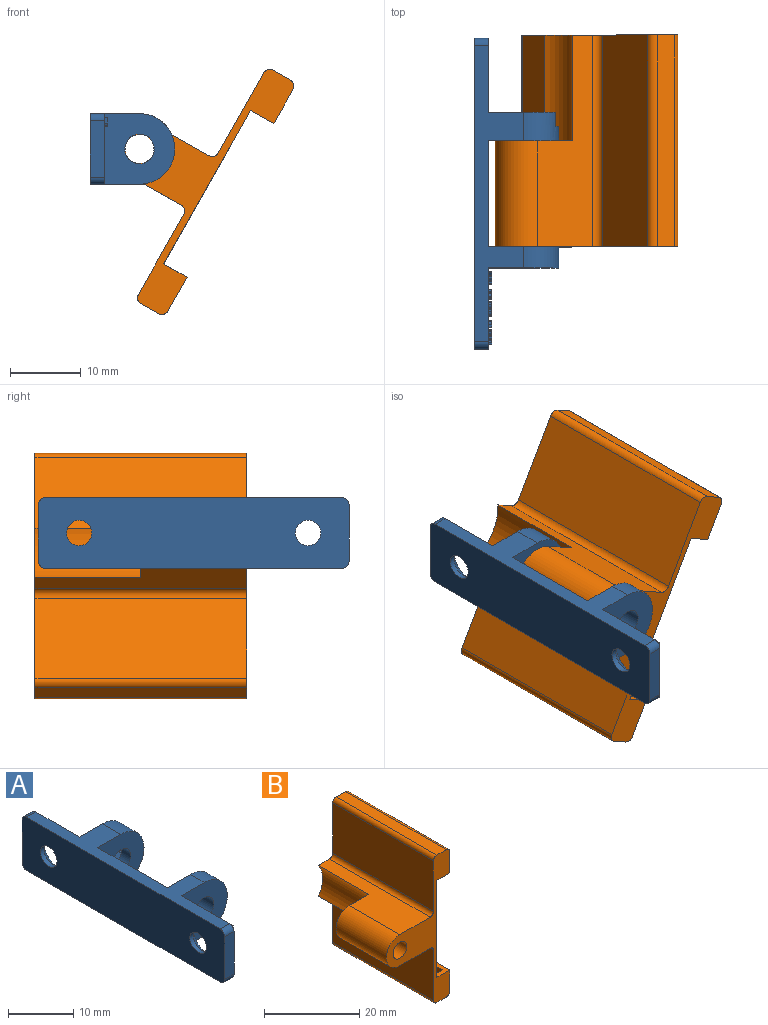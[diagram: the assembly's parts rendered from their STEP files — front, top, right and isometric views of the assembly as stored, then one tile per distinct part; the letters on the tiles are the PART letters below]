
ASSEMBLY  parts=2 mates=1
PART A: 199 faces, bbox 12x44x10 mm
  f0: plane 11.48x10mm, normal (1,0,0), area 80.2mm2, adj f4,f5,f6,f7,f8,f11,f28,f32
  f1: plane 15.05x10mm, normal (1,0,0), area 150.5mm2, adj f4,f8,f17,f29
  f2: plane 10x9.58mm, normal (0,1,0), area 42.1mm2, adj f3,f4,f8,f18,f19,f20,f21,f22
  f3: plane 10.48x10mm, normal (1,0,0), area 76mm2, adj f2,f4,f8,f12,f13,f14,f16
  f4: plane 42x7mm, normal (0,0,1), area 119mm2, adj f0,f1,f2,f3,f5,f9,f12,f17
  f5: cylinder r=1mm len=2mm, axis (-1,0,0), area 3.1mm2, adj f0,f4,f6,f9
  f6: plane 8x2mm, normal (0,-1,0), area 16mm2, adj f0,f5,f7,f9
  f7: cylinder r=1mm len=2mm, axis (-1,0,0), area 3.1mm2, adj f0,f6,f8,f9
  f8: plane 42x7mm, normal (0,0,-1), area 119mm2, adj f0,f1,f2,f3,f7,f9,f14,f17
  f9: plane 44x10mm, normal (-1,0,0), area 418.8mm2, adj f4,f5,f6,f7,f8,f10,f12,f13
  f10: cylinder r=1.8mm len=3.6mm, axis (1,0,0), area 9mm2, adj f9,f11
  f11: cone r=1.8mm half-angle=45deg, axis (1,0,0), area 25.6mm2, adj f0,f10
  f12: cylinder r=1mm len=2mm, axis (-1,0,0), area 3.1mm2, adj f3,f4,f9,f13
  f13: plane 8x2mm, normal (0,1,0), area 16mm2, adj f3,f9,f12,f14
  f14: cylinder r=1mm len=2mm, axis (-1,0,0), area 3.1mm2, adj f3,f8,f9,f13
  f15: cylinder r=1.8mm len=3.6mm, axis (1,0,0), area 9mm2, adj f9,f16
  f16: cone r=1.8mm half-angle=45deg, axis (1,0,0), area 25.6mm2, adj f3,f15
  f17: plane 10x10mm, normal (0,-1,0), area 75.4mm2, adj f1,f4,f8,f26,f27
  f18: plane 3.46x2mm, normal (-0.5,0,-0.87), area 8mm2, adj f2,f19,f24,f25
  f19: plane 2x1.12mm, normal (0,0,-1), area 2.2mm2, adj f2,f18,f25,f27
  f20: plane 2x1.12mm, normal (0,0,1), area 2.2mm2, adj f2,f21,f25,f27
  f21: plane 3.46x2mm, normal (-0.5,0,0.87), area 8mm2, adj f2,f20,f22,f25
  f22: plane 3.46x2mm, normal (0.5,0,0.87), area 8mm2, adj f2,f21,f23,f25
  f23: plane 4x2mm, normal (1,0,0), area 8mm2, adj f2,f22,f24,f25
  f24: plane 3.46x2mm, normal (0.5,0,-0.87), area 8mm2, adj f2,f18,f23,f25
  f25: plane 8.46x8mm, normal (0,1,0), area 33.3mm2, adj f18,f19,f20,f21,f22,f23,f24,f26
  f26: cylinder r=2.1mm len=4.2mm, axis (0,1,0), area 26.4mm2, adj f17,f25
  f27: cylinder r=5mm len=10mm, axis (0,1,0), area 54.6mm2, adj f2,f4,f8,f17,f19,f20,f25
  f28: plane 10x10mm, normal (0,-1,0), area 75.4mm2, adj f0,f4,f8,f30,f31
  f29: plane 10x10mm, normal (0,1,0), area 75.4mm2, adj f1,f4,f8,f30,f31
  f30: cylinder r=5mm len=10mm, axis (0,1,0), area 47.1mm2, adj f4,f8,f28,f29
  f31: cylinder r=2.1mm len=4.2mm, axis (0,1,0), area 39.6mm2, adj f28,f29
  f32: plane 0.84x0.5mm, normal (0,1,0), area 0.4mm2, adj f0,f33,f46,f47
  f33: plane 0.5x0.27mm, normal (0,0,1), area 0.1mm2, adj f0,f32,f34,f47
  f34: plane 0.79x0.5mm, normal (0,-1,0), area 0.4mm2, adj f0,f33,f35,f47
  f35: extruded ~0.5x0.22mm, area 0.1mm2, adj f0,f34,f36,f47
  f36: extruded ~0.5x0.2mm, area 0.1mm2, adj f0,f35,f37,f47
  f37: extruded ~0.5x0.2mm, area 0.1mm2, adj f0,f36,f38,f47
  f38: extruded ~0.5x0.22mm, area 0.1mm2, adj f0,f37,f39,f47
  f39: plane 0.79x0.5mm, normal (0,1,0), area 0.4mm2, adj f0,f38,f40,f47
  f40: plane 0.5x0.27mm, normal (0,0,1), area 0.1mm2, adj f0,f39,f41,f47
  f41: plane 0.83x0.5mm, normal (0,-1,0), area 0.4mm2, adj f0,f40,f42,f47
  f42: extruded ~0.5x0.35mm, area 0.2mm2, adj f0,f41,f43,f47
  f43: extruded ~0.5x0.39mm, area 0.2mm2, adj f0,f42,f44,f47
  f44: extruded ~0.5x0.29mm, area 0.1mm2, adj f0,f43,f45,f47
  f45: extruded ~0.5x0.19mm, area 0.1mm2, adj f0,f44,f46,f47
  f46: extruded ~0.5x0.25mm, area 0.1mm2, adj f0,f32,f45,f47
  f47: plane 1.31x1.06mm, normal (1,0,0), area 0.8mm2, adj f32,f33,f34,f35,f36,f37,f38,f39
  f48: extruded ~0.5x0.28mm, area 0.2mm2, adj f0,f49,f75,f76
  f49: extruded ~0.5x0.21mm, area 0.1mm2, adj f0,f48,f50,f76
  f50: extruded ~0.5x0.25mm, area 0.2mm2, adj f0,f49,f51,f76
  f51: extruded ~0.5x0.17mm, area 0.1mm2, adj f0,f50,f52,f76
  f52: extruded ~0.5x0.05mm, area 0mm2, adj f0,f51,f53,f76
  f53: extruded ~0.5x0.06mm, area 0mm2, adj f0,f52,f54,f76
  f54: extruded ~0.5x0.09mm, area 0.1mm2, adj f0,f53,f55,f76
  f55: extruded ~0.5x0.12mm, area 0.1mm2, adj f0,f54,f56,f76
  f56: extruded ~0.5x0.13mm, area 0.1mm2, adj f0,f55,f57,f76
  f57: extruded ~0.5x0.17mm, area 0.1mm2, adj f0,f56,f58,f76
  f58: plane 0.5x0.21mm, normal (0,0.92,-0.38), area 0.1mm2, adj f0,f57,f59,f76
  f59: extruded ~0.5x0.19mm, area 0.1mm2, adj f0,f58,f60,f76
  f60: extruded ~0.5x0.19mm, area 0.1mm2, adj f0,f59,f61,f76
  f61: extruded ~0.5x0.32mm, area 0.2mm2, adj f0,f60,f62,f76
  f62: extruded ~0.5x0.27mm, area 0.2mm2, adj f0,f61,f63,f76
  f63: extruded ~0.5x0.16mm, area 0.1mm2, adj f0,f62,f64,f76
  f64: extruded ~0.5x0.12mm, area 0.1mm2, adj f0,f63,f65,f76
  f65: extruded ~0.5x0.18mm, area 0.1mm2, adj f0,f64,f66,f76
  f66: extruded ~0.5x0.17mm, area 0.1mm2, adj f0,f65,f67,f76
  f67: extruded ~0.5x0.06mm, area 0mm2, adj f0,f66,f68,f76
  f68: extruded ~0.5x0.07mm, area 0mm2, adj f0,f67,f69,f76
  f69: extruded ~0.5x0.1mm, area 0.1mm2, adj f0,f68,f70,f76
  f70: extruded ~0.5x0.14mm, area 0.1mm2, adj f0,f69,f71,f76
  f71: extruded ~0.5x0.17mm, area 0.1mm2, adj f0,f70,f72,f76
  f72: extruded ~0.5x0.22mm, area 0.1mm2, adj f0,f71,f73,f76
  f73: plane 0.5x0.26mm, normal (0,-1,0), area 0.1mm2, adj f0,f72,f74,f76
  f74: extruded ~0.5x0.37mm, area 0.2mm2, adj f0,f73,f75,f76
  f75: extruded ~0.5x0.35mm, area 0.2mm2, adj f0,f48,f74,f76
  f76: plane 1.33x0.84mm, normal (1,0,0), area 0.6mm2, adj f48,f49,f50,f51,f52,f53,f54,f55
  f77: plane 0.5x0.34mm, normal (0,1,0), area 0.2mm2, adj f78,f101,f102,f103
  f78: plane 0.5x0.17mm, normal (0,0,-1), area 0.1mm2, adj f77,f79,f102,f103
  f79: extruded ~0.5x0.23mm, area 0.2mm2, adj f78,f80,f102,f103
  f80: extruded ~0.5x0.13mm, area 0.1mm2, adj f79,f81,f102,f103
  f81: extruded ~0.5x0.17mm, area 0.1mm2, adj f80,f101,f102,f103
  f82: plane 0.5x0.16mm, normal (0,0,1), area 0.1mm2, adj f83,f99,f102,f104
  f83: plane 0.5x0.29mm, normal (0,1,0), area 0.1mm2, adj f82,f84,f102,f104
  f84: plane 0.5x0.14mm, normal (0,0,-1), area 0.1mm2, adj f83,f85,f102,f104
  f85: extruded ~0.5x0.17mm, area 0.1mm2, adj f84,f86,f102,f104
  f86: extruded ~0.5x0.11mm, area 0.1mm2, adj f85,f87,f102,f104
  f87: extruded ~0.5x0.11mm, area 0.1mm2, adj f86,f99,f102,f104
  f88: plane 0.5x0.4mm, normal (0,0,1), area 0.2mm2, adj f0,f89,f100,f102
  f89: plane 1.3x0.5mm, normal (0,-1,0), area 0.6mm2, adj f0,f88,f90,f102
  f90: plane 0.5x0.48mm, normal (0,0,-1), area 0.2mm2, adj f0,f89,f91,f102
  f91: extruded ~0.5x0.35mm, area 0.2mm2, adj f0,f90,f92,f102
  f92: extruded ~0.5x0.28mm, area 0.2mm2, adj f0,f91,f93,f102
  f93: extruded ~0.5x0.2mm, area 0.1mm2, adj f0,f92,f94,f102
  f94: extruded ~0.5x0.18mm, area 0.1mm2, adj f0,f93,f95,f102
  f95: plane 0.5x0.01mm, normal (0,1,0), area 0mm2, adj f0,f94,f96,f102
  f96: extruded ~0.5x0.15mm, area 0.1mm2, adj f0,f95,f97,f102
  f97: extruded ~0.5x0.19mm, area 0.1mm2, adj f0,f96,f98,f102
  f98: extruded ~0.5x0.25mm, area 0.1mm2, adj f0,f97,f100,f102
  f99: extruded ~0.5x0.16mm, area 0.1mm2, adj f82,f87,f102,f104
  f100: extruded ~0.5x0.4mm, area 0.2mm2, adj f0,f88,f98,f102
  f101: plane 0.5x0.18mm, normal (0,0,1), area 0.1mm2, adj f77,f81,f102,f103
  f102: plane 1.3x0.96mm, normal (1,0,0), area 0.9mm2, adj f77,f78,f79,f80,f81,f82,f83,f84
  f103: plane 0.4x0.34mm, normal (1,0,0), area 0.1mm2, adj f77,f78,f79,f80,f81,f101
  f104: plane 0.37x0.29mm, normal (1,0,0), area 0.1mm2, adj f82,f83,f84,f85,f86,f87,f99
  f105: extruded ~0.5x0.24mm, area 0.1mm2, adj f0,f106,f119,f120
  f106: extruded ~0.5x0.14mm, area 0.1mm2, adj f0,f105,f107,f120
  f107: extruded ~0.5x0.15mm, area 0.1mm2, adj f0,f106,f108,f120
  f108: plane 0.5x0.22mm, normal (0,0.93,-0.37), area 0.1mm2, adj f0,f107,f109,f120
  f109: extruded ~0.5x0.38mm, area 0.2mm2, adj f0,f108,f110,f120
  f110: extruded ~0.5x0.32mm, area 0.2mm2, adj f0,f109,f111,f120
  f111: extruded ~0.5x0.23mm, area 0.2mm2, adj f0,f110,f112,f120
  f112: extruded ~0.5x0.35mm, area 0.2mm2, adj f0,f111,f113,f120
  f113: extruded ~0.5x0.49mm, area 0.3mm2, adj f0,f112,f114,f120
  f114: extruded ~0.5x0.43mm, area 0.2mm2, adj f0,f113,f115,f120
  f115: extruded ~0.5x0.36mm, area 0.2mm2, adj f0,f114,f116,f120
  f116: plane 0.5x0.23mm, normal (0,1,0), area 0.1mm2, adj f0,f115,f117,f120
  f117: extruded ~0.5x0.33mm, area 0.2mm2, adj f0,f116,f118,f120
  f118: extruded ~0.5x0.43mm, area 0.3mm2, adj f0,f117,f119,f120
  f119: extruded ~0.5x0.32mm, area 0.2mm2, adj f0,f105,f118,f120
  f120: plane 1.33x0.99mm, normal (1,0,0), area 0.6mm2, adj f105,f106,f107,f108,f109,f110,f111,f112
  f121: plane 0.5x0.1mm, normal (0,0.04,-1), area 0.1mm2, adj f122,f145,f146,f147
  f122: plane 0.5x0.08mm, normal (0,-1,0), area 0mm2, adj f121,f123,f146,f147
  f123: extruded ~0.5x0.14mm, area 0.1mm2, adj f122,f124,f146,f147
  f124: extruded ~0.5x0.15mm, area 0.1mm2, adj f123,f125,f146,f147
  f125: extruded ~0.5x0.13mm, area 0.1mm2, adj f124,f126,f146,f147
  f126: extruded ~0.5x0.12mm, area 0.1mm2, adj f125,f145,f146,f147
  f127: plane 0.5x0.13mm, normal (0,-0.93,-0.36), area 0.1mm2, adj f0,f128,f144,f146
  f128: plane 0.5x0.19mm, normal (0,0,-1), area 0.1mm2, adj f0,f127,f129,f146
  f129: plane 0.66x0.5mm, normal (0,1,0), area 0.3mm2, adj f0,f128,f130,f146
  f130: extruded ~0.5x0.26mm, area 0.1mm2, adj f0,f129,f131,f146
  f131: extruded ~0.5x0.31mm, area 0.2mm2, adj f0,f130,f132,f146
  f132: extruded ~0.5x0.38mm, area 0.2mm2, adj f0,f131,f133,f146
  f133: plane 0.5x0.18mm, normal (0,-0.9,-0.44), area 0.1mm2, adj f0,f132,f134,f146
  f134: extruded ~0.5x0.28mm, area 0.1mm2, adj f0,f133,f135,f146
  f135: extruded ~0.5x0.15mm, area 0.1mm2, adj f0,f134,f136,f146
  f136: plane 0.5x0.04mm, normal (0,-1,0), area 0mm2, adj f0,f135,f137,f146
  f137: plane 0.5x0.17mm, normal (0,-0.03,1), area 0.1mm2, adj f0,f136,f138,f146
  f138: extruded ~0.5x0.33mm, area 0.2mm2, adj f0,f137,f139,f146
  f139: extruded ~0.5x0.23mm, area 0.1mm2, adj f0,f138,f140,f146
  f140: extruded ~0.5x0.23mm, area 0.1mm2, adj f0,f139,f141,f146
  f141: extruded ~0.5x0.22mm, area 0.1mm2, adj f0,f140,f142,f146
  f142: extruded ~0.5x0.19mm, area 0.1mm2, adj f0,f141,f143,f146
  f143: extruded ~0.5x0.14mm, area 0.1mm2, adj f0,f142,f144,f146
  f144: plane 0.5x0.01mm, normal (0,0,-1), area 0mm2, adj f0,f127,f143,f146
  f145: extruded ~0.5x0.18mm, area 0.1mm2, adj f121,f126,f146,f147
  f146: plane 1.03x0.88mm, normal (1,0,0), area 0.6mm2, adj f121,f122,f123,f124,f125,f126,f127,f128
  f147: plane 0.34x0.28mm, normal (1,0,0), area 0.1mm2, adj f121,f122,f123,f124,f125,f126,f145
  f148: plane 0.5x0.27mm, normal (0,0,-1), area 0.1mm2, adj f0,f149,f175,f176
  f149: plane 0.5x0.5mm, normal (0,1,0), area 0.2mm2, adj f0,f148,f150,f176
  f150: extruded ~0.5x0.23mm, area 0.1mm2, adj f0,f149,f151,f176
  f151: extruded ~0.5x0.15mm, area 0.1mm2, adj f0,f150,f152,f176
  f152: extruded ~0.5x0.11mm, area 0.1mm2, adj f0,f151,f153,f176
  f153: extruded ~0.5x0.16mm, area 0.1mm2, adj f0,f152,f154,f176
  f154: plane 0.58x0.5mm, normal (0,-1,0), area 0.3mm2, adj f0,f153,f155,f176
  f155: plane 0.5x0.27mm, normal (0,0,-1), area 0.1mm2, adj f0,f154,f156,f176
  f156: plane 0.65x0.5mm, normal (0,1,0), area 0.3mm2, adj f0,f155,f157,f176
  f157: extruded ~0.5x0.28mm, area 0.1mm2, adj f0,f156,f158,f176
  f158: extruded ~0.5x0.25mm, area 0.1mm2, adj f0,f157,f159,f176
  f159: extruded ~0.5x0.18mm, area 0.1mm2, adj f0,f158,f160,f176
  f160: extruded ~0.5x0.12mm, area 0.1mm2, adj f0,f159,f161,f176
  f161: plane 0.5x0.02mm, normal (0,0,1), area 0mm2, adj f0,f160,f162,f176
  f162: extruded ~0.5x0.3mm, area 0.2mm2, adj f0,f161,f163,f176
  f163: extruded ~0.5x0.17mm, area 0.1mm2, adj f0,f162,f164,f176
  f164: extruded ~0.5x0.12mm, area 0.1mm2, adj f0,f163,f165,f176
  f165: plane 0.5x0.02mm, normal (0,0,1), area 0mm2, adj f0,f164,f166,f176
  f166: plane 0.5x0.13mm, normal (0,0.96,0.28), area 0.1mm2, adj f0,f165,f167,f176
  f167: plane 0.5x0.21mm, normal (0,0,1), area 0.1mm2, adj f0,f166,f168,f176
  f168: plane 0.99x0.5mm, normal (0,-1,0), area 0.5mm2, adj f0,f167,f169,f176
  f169: plane 0.5x0.27mm, normal (0,0,-1), area 0.1mm2, adj f0,f168,f170,f176
  f170: plane 0.5x0.47mm, normal (0,1,0), area 0.2mm2, adj f0,f169,f171,f176
  f171: extruded ~0.5x0.25mm, area 0.1mm2, adj f0,f170,f172,f176
  f172: extruded ~0.5x0.15mm, area 0.1mm2, adj f0,f171,f173,f176
  f173: extruded ~0.5x0.11mm, area 0.1mm2, adj f0,f172,f174,f176
  f174: extruded ~0.5x0.16mm, area 0.1mm2, adj f0,f173,f175,f176
  f175: plane 0.58x0.5mm, normal (0,-1,0), area 0.3mm2, adj f0,f148,f174,f176
  f176: plane 1.5x1.01mm, normal (1,0,0), area 0.9mm2, adj f148,f149,f150,f151,f152,f153,f154,f155
  f177: plane 0.5x0.28mm, normal (0,0,1), area 0.1mm2, adj f0,f178,f186,f187
  f178: plane 0.77x0.5mm, normal (0,-0.95,0.3), area 0.4mm2, adj f0,f177,f179,f187
  f179: extruded ~0.5x0.29mm, area 0.1mm2, adj f0,f178,f180,f187
  f180: extruded ~0.5x0.13mm, area 0.1mm2, adj f0,f179,f181,f187
  f181: extruded ~0.5x0.16mm, area 0.1mm2, adj f0,f180,f182,f187
  f182: plane 0.77x0.5mm, normal (0,0.95,0.3), area 0.4mm2, adj f0,f181,f183,f187
  f183: plane 0.5x0.28mm, normal (0,0,1), area 0.1mm2, adj f0,f182,f184,f187
  f184: plane 1.3x0.5mm, normal (0,-0.95,-0.32), area 0.7mm2, adj f0,f183,f185,f187
  f185: plane 0.5x0.3mm, normal (0,0,-1), area 0.1mm2, adj f0,f184,f186,f187
  f186: plane 1.3x0.5mm, normal (0,0.95,-0.32), area 0.7mm2, adj f0,f177,f185,f187
  f187: plane 1.3x1.18mm, normal (1,0,0), area 0.6mm2, adj f177,f178,f179,f180,f181,f182,f183,f184
  f188: plane 0.5x0.27mm, normal (0,0,-1), area 0.1mm2, adj f0,f189,f197,f198
  f189: plane 1.3x0.5mm, normal (0,1,0), area 0.6mm2, adj f0,f188,f190,f198
  f190: plane 0.5x0.23mm, normal (0,0,1), area 0.1mm2, adj f0,f189,f191,f198
  f191: plane 0.5x0.42mm, normal (0,-0.62,0.78), area 0.3mm2, adj f0,f190,f192,f198
  f192: plane 0.5x0.16mm, normal (0,-0.78,-0.63), area 0.1mm2, adj f0,f191,f193,f198
  f193: plane 0.5x0.15mm, normal (0,0.63,-0.78), area 0.1mm2, adj f0,f192,f194,f198
  f194: extruded ~0.5x0.09mm, area 0.1mm2, adj f0,f193,f195,f198
  f195: plane 0.5x0.13mm, normal (0,-1,0.03), area 0.1mm2, adj f0,f194,f196,f198
  f196: plane 0.5x0.12mm, normal (0,-1,0.02), area 0.1mm2, adj f0,f195,f197,f198
  f197: plane 0.75x0.5mm, normal (0,-1,0), area 0.4mm2, adj f0,f188,f196,f198
  f198: plane 1.3x0.64mm, normal (1,0,0), area 0.4mm2, adj f188,f189,f190,f191,f192,f193,f194,f195
PART B: 33 faces, bbox 18.8x30x38 mm
  f0: plane 30x9mm, normal (0,0,-1), area 183.8mm2, adj f2,f19,f20,f28,f31,f32
  f1: cylinder r=2.05mm len=15mm, axis (0,1,0), area 193.2mm2, adj f28,f32
  f2: plane 38x9.06mm, normal (0,1,0), area 86.2mm2, adj f0,f3,f4,f5,f6,f7,f8,f9
  f3: plane 34.6x30mm, normal (1,0,0), area 1028.4mm2, adj f2,f6,f11,f26,f27,f28,f29,f30
  f4: plane 29x2.4mm, normal (0,0,-1), area 69.6mm2, adj f2,f6,f7,f30
  f5: plane 29x4.8mm, normal (-1,0,0), area 139.2mm2, adj f2,f7,f27,f30
  f6: cylinder r=0.2mm len=29mm, axis (0,1,0), area 9.1mm2, adj f2,f3,f4,f30
  f7: cylinder r=0.2mm len=29mm, axis (0,1,0), area 9.1mm2, adj f2,f4,f5,f30
  f8: plane 29x4.8mm, normal (-1,0,0), area 139.2mm2, adj f2,f10,f26,f29
  f9: plane 29x2.4mm, normal (0,0,1), area 69.6mm2, adj f2,f10,f11,f29
  f10: cylinder r=0.2mm len=29mm, axis (0,1,0), area 9.1mm2, adj f2,f8,f9,f29
  f11: cylinder r=0.2mm len=29mm, axis (0,1,0), area 9.1mm2, adj f2,f3,f9,f29
  f12: plane 30x5.5mm, normal (1,0,0), area 165mm2, adj f2,f13,f27,f28
  f13: cylinder r=1mm len=30mm, axis (0,1,0), area 47.1mm2, adj f2,f12,f14,f28
  f14: plane 30x2.8mm, normal (0,0,1), area 84mm2, adj f2,f13,f15,f28
  f15: cylinder r=1mm len=30mm, axis (0,1,0), area 47.1mm2, adj f2,f14,f16,f28
  f16: plane 30x13mm, normal (-1,0,0), area 390mm2, adj f2,f15,f17,f28
  f17: cylinder r=1mm len=30mm, axis (0,1,0), area 47.1mm2, adj f2,f16,f18,f28
  f18: plane 30x9mm, normal (0,0,1), area 183.8mm2, adj f2,f17,f19,f28,f31,f32
  f19: cylinder r=4mm len=15mm, axis (0,1,0), area 188.5mm2, adj f0,f18,f28,f32
  f20: cylinder r=1mm len=30mm, axis (0,1,0), area 47.1mm2, adj f0,f2,f21,f28
  f21: plane 30x13mm, normal (-1,0,0), area 390mm2, adj f2,f20,f22,f28
  f22: cylinder r=1mm len=30mm, axis (0,1,0), area 47.1mm2, adj f2,f21,f23,f28
  f23: plane 30x2.8mm, normal (0,0,-1), area 84mm2, adj f2,f22,f24,f28
  f24: cylinder r=1mm len=30mm, axis (0,1,0), area 47.1mm2, adj f2,f23,f25,f28
  f25: plane 30x5.5mm, normal (1,0,0), area 165mm2, adj f2,f24,f26,f28
  f26: plane 30x3.8mm, normal (0,0,1), area 32.8mm2, adj f2,f3,f8,f25,f28,f29
  f27: plane 30x3.8mm, normal (0,0,-1), area 32.8mm2, adj f2,f3,f5,f12,f28,f30
  f28: plane 38x18.8mm, normal (0,-1,0), area 178.9mm2, adj f0,f1,f3,f12,f13,f14,f15,f16
  f29: plane 5x2.8mm, normal (0,1,0), area 14mm2, adj f3,f8,f9,f10,f11,f26
  f30: plane 5x2.8mm, normal (0,1,0), area 14mm2, adj f3,f4,f5,f6,f7,f27
  f31: cylinder r=7mm len=15mm, axis (0,1,0), area 127.7mm2, adj f0,f2,f18,f32
  f32: plane 11x8mm, normal (0,1,0), area 64.7mm2, adj f0,f1,f18,f19,f31
PLACE A t=(-16.92,-14.39,8.6)mm
PLACE B rot(axis=(0,1,0),29.5deg) t=(-1.21,8.09,8.68)mm
MATE revolute A.f26 <-> B.f1  axis (0,1,0) through (-9.92,-21.91,13.6)mm
